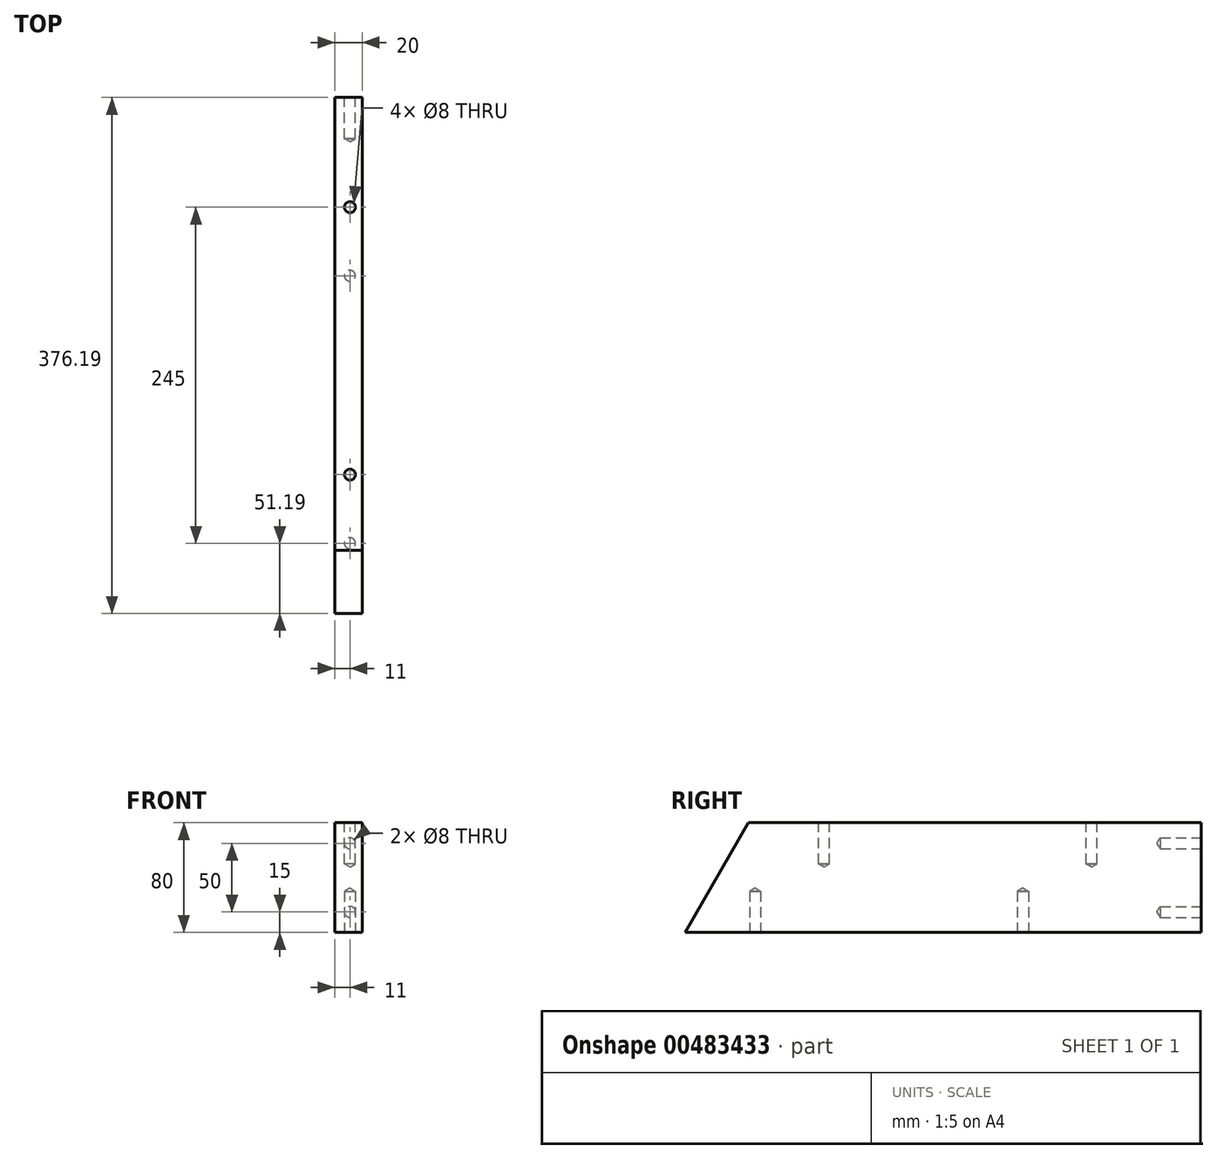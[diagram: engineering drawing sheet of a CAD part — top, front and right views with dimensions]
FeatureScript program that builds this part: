
annotation { "Feature Type Name" : "Feature", "Feature Type Description" : "" }
export const myFeature = defineFeature(function(context is Context, id is Id, definition is map)
    precondition{}
    {
        {
            var Q0;
            Q0=qCreatedBy(makeId("Right.planeOp"),FACE);
            var sketch = newSketch(context, id + "F0", { "sketchPlane" : qUnion([Q0])});
            skLineSegment(sketch, "E0", {"start": v(0, 0) * mm, "end": v(-376.19, 0) * mm});
            skLineSegment(sketch, "E1", {"start": v(-376.19, 0) * mm, "end": v(-330, 80) * mm});
            skLineSegment(sketch, "E2", {"start": v(-330, 80) * mm, "end": v(0, 80) * mm});
            skLineSegment(sketch, "E3", {"start": v(0, 80) * mm, "end": v(0, 0) * mm});
            skSolve(sketch);
        }
        {
            var Q0;
            Q0=qSketchRegion(id+"F0",true);
            extrude(context, id + "F1", {"entities" : qUnion([Q0]), "depth" : 20 * mm});
        }
        {
            var Q0;
            Q0=makeQuery(id+"F1.opExtrude","SWEPT_FACE",FACE,{"disambiguationData":[OSD([sQuery(id+"F0.wireOp",EDGE,"E0")])]});
            var sketch = newSketch(context, id + "F2", { "sketchPlane" : qUnion([Q0])});
            skPoint(sketch, "E4", {"position": v(11, 130) * mm});
            skPoint(sketch, "E5", {"position": v(11, 325) * mm});
            skSolve(sketch);
        }
        {
            var Q0;
            Q0=makeQuery(id+"F1.opExtrude","SWEPT_FACE",FACE,{"disambiguationData":[OSD([sQuery(id+"F0.wireOp",EDGE,"E3")])]});
            var sketch = newSketch(context, id + "F3", { "sketchPlane" : qUnion([Q0])});
            skPoint(sketch, "E6", {"position": v(-11, 15) * mm});
            skPoint(sketch, "E7", {"position": v(-11, 65) * mm});
            skSolve(sketch);
        }
        {
            var Q0;
            Q0=makeQuery(id+"F1.opExtrude","SWEPT_FACE",FACE,{"disambiguationData":[OSD([sQuery(id+"F0.wireOp",EDGE,"E2")])]});
            var sketch = newSketch(context, id + "F4", { "sketchPlane" : qUnion([Q0])});
            skPoint(sketch, "E8", {"position": v(11, -80) * mm});
            skPoint(sketch, "E9", {"position": v(11, -275) * mm});
            skSolve(sketch);
        }
        {
            var Q0;
            Q0=sQuery(id+"F2.wireOp",VERTEX,"E5");
            var Q1;
            Q1=sQuery(id+"F2.wireOp",VERTEX,"E4");
            var Q2;
            Q2=sQuery(id+"F3.wireOp",VERTEX,"E6");
            var Q3;
            Q3=sQuery(id+"F3.wireOp",VERTEX,"E7");
            var Q4;
            Q4=sQuery(id+"F4.wireOp",VERTEX,"E9");
            var Q5;
            Q5=sQuery(id+"F4.wireOp",VERTEX,"E8");
            var Q6;
            Q6=makeQuery(id+"F1.opExtrude","SWEPT_BODY",BODY,{"disambiguationData":[OSD([sQuery(id+"F0.wireOp",EDGE,"E0"),sQuery(id+"F0.wireOp",EDGE,"E1"),sQuery(id+"F0.wireOp",EDGE,"E2"),sQuery(id+"F0.wireOp",EDGE,"E3")])]});
            hole(context, id + "F5", {"style" : HoleStyle.SIMPLE, "endStyle" : HoleEndStyle.BLIND, "standardTappedOrClearance" : lookupTablePath({ "standard" : "ISO", "size" : "8", "type" : "Drilled" }), "standardBlindInLast" : lookupTablePath({ "standard" : "ISO", "size" : "8", "type" : "Drilled" }), "holeDiameter" : 8 * mm, "holeDepth" : 30 * mm, "isTappedThrough" : true, "tappedDepth" : 12 * mm, "tapClearance" : 3, "locations" : qUnion([Q0, Q1, Q2, Q3, Q4, Q5]), "scope" : qUnion([Q6])});
        }
    });
